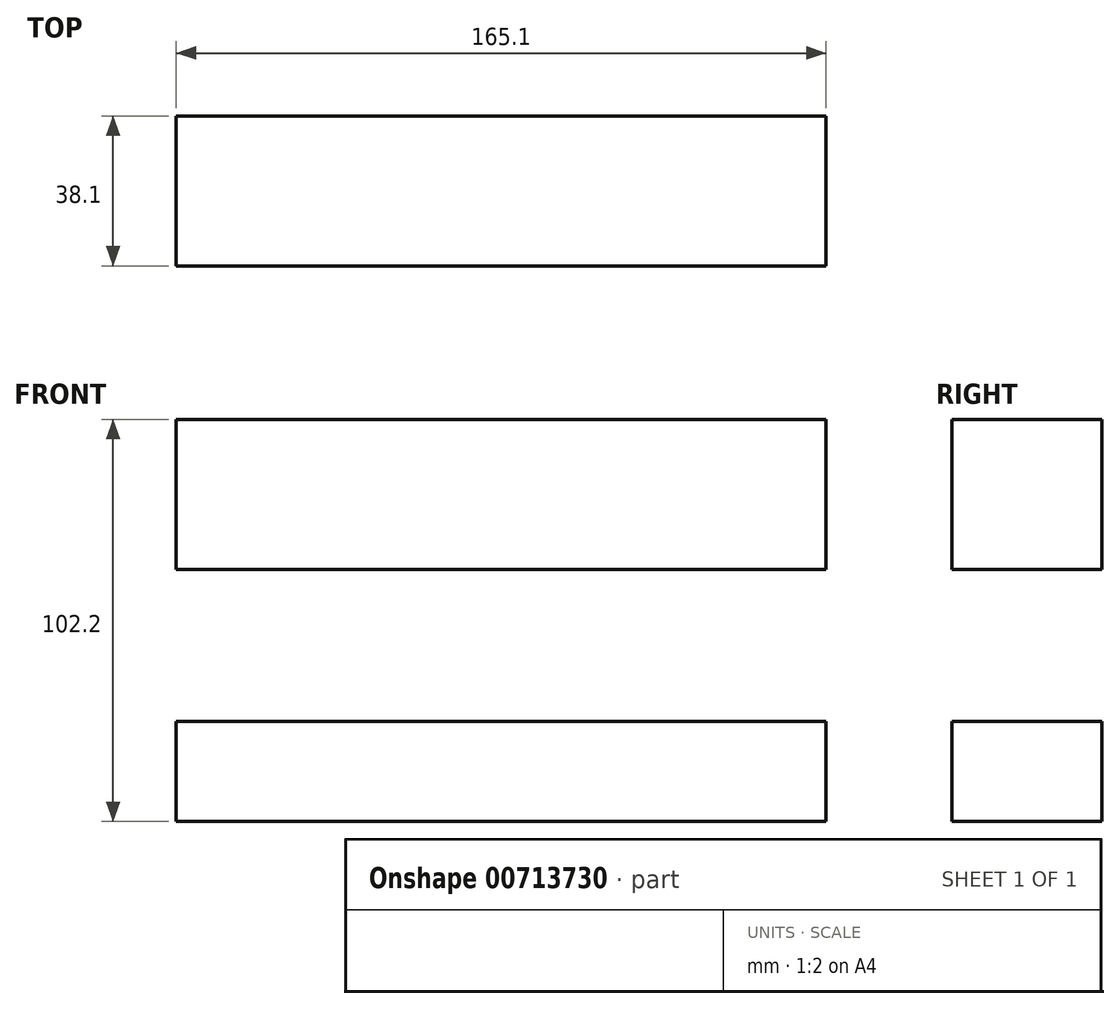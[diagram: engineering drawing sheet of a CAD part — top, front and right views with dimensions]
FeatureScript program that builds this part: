
annotation { "Feature Type Name" : "Feature", "Feature Type Description" : "" }
export const myFeature = defineFeature(function(context is Context, id is Id, definition is map)
    precondition{}
    {
        {
            var Q0;
            Q0=qCreatedBy(makeId("Front.planeOp"),FACE);
            var sketch = newSketch(context, id + "F0", { "sketchPlane" : qUnion([Q0])});
            skLineSegment(sketch, "E0.bottom", {"start": v(0, -6.73) * mm, "end": v(-82.55, -6.73) * mm});
            skLineSegment(sketch, "E0.top", {"start": v(0, -44.83) * mm, "end": v(-82.55, -44.83) * mm});
            skLineSegment(sketch, "E0.left", {"start": v(0, -6.73) * mm, "end": v(0, -44.83) * mm});
            skLineSegment(sketch, "E0.right", {"start": v(-82.55, -6.73) * mm, "end": v(-82.55, -44.83) * mm});
            skLineSegment(sketch, "E1.bottom", {"start": v(0, -6.73) * mm, "end": v(82.55, -6.73) * mm});
            skLineSegment(sketch, "E1.top", {"start": v(0, -44.83) * mm, "end": v(82.55, -44.83) * mm});
            skLineSegment(sketch, "E1.right", {"start": v(82.55, -6.73) * mm, "end": v(82.55, -44.83) * mm});
            skLineSegment(sketch, "E2.bottom", {"start": v(0, -6.73) * mm, "end": v(-19.05, -6.73) * mm});
            skLineSegment(sketch, "E2.top", {"start": v(0, 120.27) * mm, "end": v(-19.05, 120.27) * mm});
            skLineSegment(sketch, "E2.left", {"start": v(0, -6.73) * mm, "end": v(0, 120.27) * mm});
            skLineSegment(sketch, "E2.right", {"start": v(-19.05, -6.73) * mm, "end": v(-19.05, 120.27) * mm});
            skLineSegment(sketch, "E3.bottom", {"start": v(0, -6.73) * mm, "end": v(19.05, -6.73) * mm});
            skLineSegment(sketch, "E3.top", {"start": v(0, 120.27) * mm, "end": v(19.05, 120.27) * mm});
            skLineSegment(sketch, "E3.right", {"start": v(19.05, -6.73) * mm, "end": v(19.05, 120.27) * mm});
            skLineSegment(sketch, "E4.bottom", {"start": v(0, -44.83) * mm, "end": v(19.05, -44.83) * mm});
            skLineSegment(sketch, "E4.top", {"start": v(0, -85.03) * mm, "end": v(19.05, -85.03) * mm});
            skLineSegment(sketch, "E4.left", {"start": v(0, -44.83) * mm, "end": v(0, -85.03) * mm});
            skLineSegment(sketch, "E4.right", {"start": v(19.05, -44.83) * mm, "end": v(19.05, -85.03) * mm});
            skLineSegment(sketch, "E5.bottom", {"start": v(0, -44.83) * mm, "end": v(-19.05, -44.83) * mm});
            skLineSegment(sketch, "E5.top", {"start": v(0, -83.53) * mm, "end": v(-19.05, -83.53) * mm});
            skLineSegment(sketch, "E5.left", {"start": v(0, -44.83) * mm, "end": v(0, -83.53) * mm});
            skLineSegment(sketch, "E5.right", {"start": v(-19.05, -44.83) * mm, "end": v(-19.05, -83.53) * mm});
            skLineSegment(sketch, "E6.bottom", {"start": v(0, -83.53) * mm, "end": v(82.55, -83.53) * mm});
            skLineSegment(sketch, "E6.top", {"start": v(0, -108.93) * mm, "end": v(82.55, -108.93) * mm});
            skLineSegment(sketch, "E6.left", {"start": v(0, -83.53) * mm, "end": v(0, -108.93) * mm});
            skLineSegment(sketch, "E6.right", {"start": v(82.55, -83.53) * mm, "end": v(82.55, -108.93) * mm});
            skLineSegment(sketch, "E7.bottom", {"start": v(0, -83.53) * mm, "end": v(-82.55, -83.53) * mm});
            skLineSegment(sketch, "E7.top", {"start": v(0, -108.93) * mm, "end": v(-82.55, -108.93) * mm});
            skLineSegment(sketch, "E7.right", {"start": v(-82.55, -83.53) * mm, "end": v(-82.55, -108.93) * mm});
            skSolve(sketch);
        }
        {
            var Q0;
            {var subQ5=sQuery(id+"F0.wireOp",EDGE,"E4.top");Q0=makeQuery(id+"F0.imprint","IMPRINT",FACE,{"disambiguationData":[TD([[makeQuery(id+"F0.imprint","IMPRINT",EDGE,{"derivedFrom":subQ5}),-1.0]])]});}
            var Q1;
            Q1=makeQuery(id+"F0.imprint","IMPRINT",FACE,{"disambiguationData":[TD([[makeQuery(id+"F0.imprint","IMPRINT",EDGE,{"derivedFrom":sQuery(id+"F0.wireOp",EDGE,"E0.bottom")}),1.0]])]});
            var Q2;
            Q2=makeQuery(id+"F0.imprint","IMPRINT",FACE,{"disambiguationData":[TD([[makeQuery(id+"F0.imprint","IMPRINT",EDGE,{"derivedFrom":sQuery(id+"F0.wireOp",EDGE,"E1.bottom")}),-1.0]])]});
            var Q3;
            {var subQ0=sQuery(id+"F0.wireOp",EDGE,"E4.bottom");Q3=makeQuery(id+"F0.imprint","IMPRINT",FACE,{"disambiguationData":[TD([[makeQuery(id+"F0.imprint","IMPRINT",EDGE,{"derivedFrom":subQ0}),-1.0]])]});}
            var Q4;
            Q4=makeQuery(id+"F0.imprint","IMPRINT",FACE,{"disambiguationData":[TD([[makeQuery(id+"F0.imprint","IMPRINT",EDGE,{"derivedFrom":sQuery(id+"F0.wireOp",EDGE,"E5.bottom")}),1.0]])]});
            var Q5;
            Q5=makeQuery(id+"F0.imprint","IMPRINT",FACE,{"disambiguationData":[TD([[makeQuery(id+"F0.imprint","IMPRINT",EDGE,{"derivedFrom":sQuery(id+"F0.wireOp",EDGE,"E3.bottom")}),1.0]])]});
            var Q6;
            {var subQ4=sQuery(id+"F0.wireOp",EDGE,"E7.top");Q6=makeQuery(id+"F0.imprint","IMPRINT",FACE,{"disambiguationData":[TD([[makeQuery(id+"F0.imprint","IMPRINT",EDGE,{"derivedFrom":subQ4}),-1.0]])]});}
            var Q7;
            Q7=makeQuery(id+"F0.imprint","IMPRINT",FACE,{"disambiguationData":[TD([[makeQuery(id+"F0.imprint","IMPRINT",EDGE,{"derivedFrom":sQuery(id+"F0.wireOp",EDGE,"E2.bottom")}),-1.0]])]});
            var Q8;
            {var subQ0=sQuery(id+"F0.wireOp",EDGE,"E4.top");Q8=makeQuery(id+"F0.imprint","IMPRINT",FACE,{"disambiguationData":[TD([[makeQuery(id+"F0.imprint","IMPRINT",EDGE,{"derivedFrom":subQ0}),1.0]])]});}
            extrude(context, id + "F1", {"entities" : qUnion([Q0, Q1, Q2, Q3, Q4, Q5, Q6, Q7, Q8]), "depth" : 38.1 * mm, "offsetDistance" : 25.4 * mm});
        }
    });
